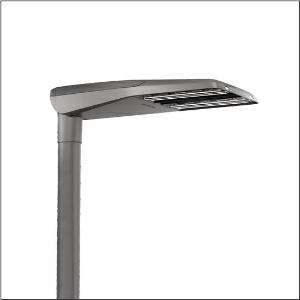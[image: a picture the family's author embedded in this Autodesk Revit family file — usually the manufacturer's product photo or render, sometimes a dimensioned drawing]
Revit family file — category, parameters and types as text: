
# Revit family: streetlight_sl_11_iq_midi___st1_0ab_5xc3n41f08me_2825
name_source: partatom
category: Lighting Fixtures
units: mm (PartAtom-declared; Revit-internal decimal feet)

## family parameters
Cut with Voids When Loaded = No
Host = Face
Light Source = No
Part Type = Normal
Room Calculation Point = No
Round Connector Dimension = Use Diameter
Shared = No

## types (1)
- --- (1 x LED, 15930 lm, 124.7 W, 4000K)
    Apparent Load = 125 VA
    CIE Flux Codes = 29 63 95 100 100
    Color Rendering = 70
    Color Temperature = 4000K
    Default Elevation = 1800 mm
    Description = Streetlight SL 11 iQ midi, mast luminaire, primary light control with 3 zone facetted reflector, of plastic, silver coated, highly specular, primary optical cover: cover, of PMMA, transparent, light distribution: ST1.0aB, light emission: direct distribution, primary light characteristic: asymmetric, installation type: post-top, side-entry, LED, High Power LED, rated luminous flux: 15.930lm, luminous efficacy: 128lm/W, light colour: 740, colour temperature: 4000K, control: optimised constant luminous flux control (CLO 2.0), Street-Remote, Desk-Remote (wireless, voltage-free reading and setting of iQ features in the workshop via application-optimized NFC function/RFID function), Light-Fading, Smart-Wire, Night-Set, Lumen-Switch, Temp-Guard, Auto-Match, with cable H07RN-F 5x 1.5mm², mains connection: 230..240V, AC, 50/60Hz, connection cable pre-assembled, cable length: 12,5m, start of lifetime: 125W, end of service life: 132W, reduction: 57W, luminaire housing, of diecast aluminium, powder-coated, Siteco® metallic grey (DB 702S), please order mast flange separately, inclination adjustable without tools: 0°, 5°, 10°, 15° (post-top) | 0°, -5°, -10°, -15° (side-entry), sealing non-destructively replaceable, multi-level sealing system, length: 780mm, width: 376mm, height: 118mm, mast flange for spigot size: 42mm (side-entry): 5XC10008XM4, 60/48mm (side-entry/post-top): 5XC10108XM2, 76/60mm (side-entry/post-top): 5XC10108XM1, equipment: Power, protection rating (complete): IP66, insulation class (complete): insulation class II (safety insulation), certification: CE, ENEC, VDE, impact resistance: IK09, permissible operating ambient temperature for outdoor applications: -25..+50°C, standard-compliant lighting for roads and squares, Environmental Product Declaration (EPD) tested and certified by an independent institute, packaging unit: 1 piece

Light Distribution: ST1.0aB
    Height = 118 mm
    Lamp = 1 x LED
    Lamp Light Flux = 15930 lm
    Lamp Power = 124.7 W
    Lamp count = 1
    Length = 780 mm
    Luminous efficacy = 128 lm/W
    Manufacturer = Siteco
    ModVariant = No
    Model = 5XC3N41F08ME
    Number of Poles = 1
    OnlyDefault = Yes
    Power Factor = 1
    Product Name = Streetlight SL 11 iQ midi | ST1.0aB
    Product group = mast luminaire | pylon top
    ProductGroupID = 6100
    Protection Class = Protection class II
    Protection Degree = IP 66
    RLX_Detail_Level = 1
    RLX_Emergency_Light_Flux = 0 lm
    RLX_Emergency_Type = 0
    RLX_Emergency_Type_DB = No
    RlxData = <blob elided: 70205 chars, md5=9e07653d>
    Socket = socket
    Standby Power = 0 W
    System Light Flux = 15930 lm
    System Power = 125 W
    Type Comments = factory setting: luminous flux: 100 % | dim-lin: 254 | 557 mA
    Type Image = l_1005960.jpg
    URL = http://relux.com
    VarID = @adj_038899
    Voltage = 0 V
    Weight = 0.00 kg
    Width = 376 mm

## geometry (parser evidence)
native form markers: Blend x4, Sweep x10
no freeform markers — native parametric forms only
